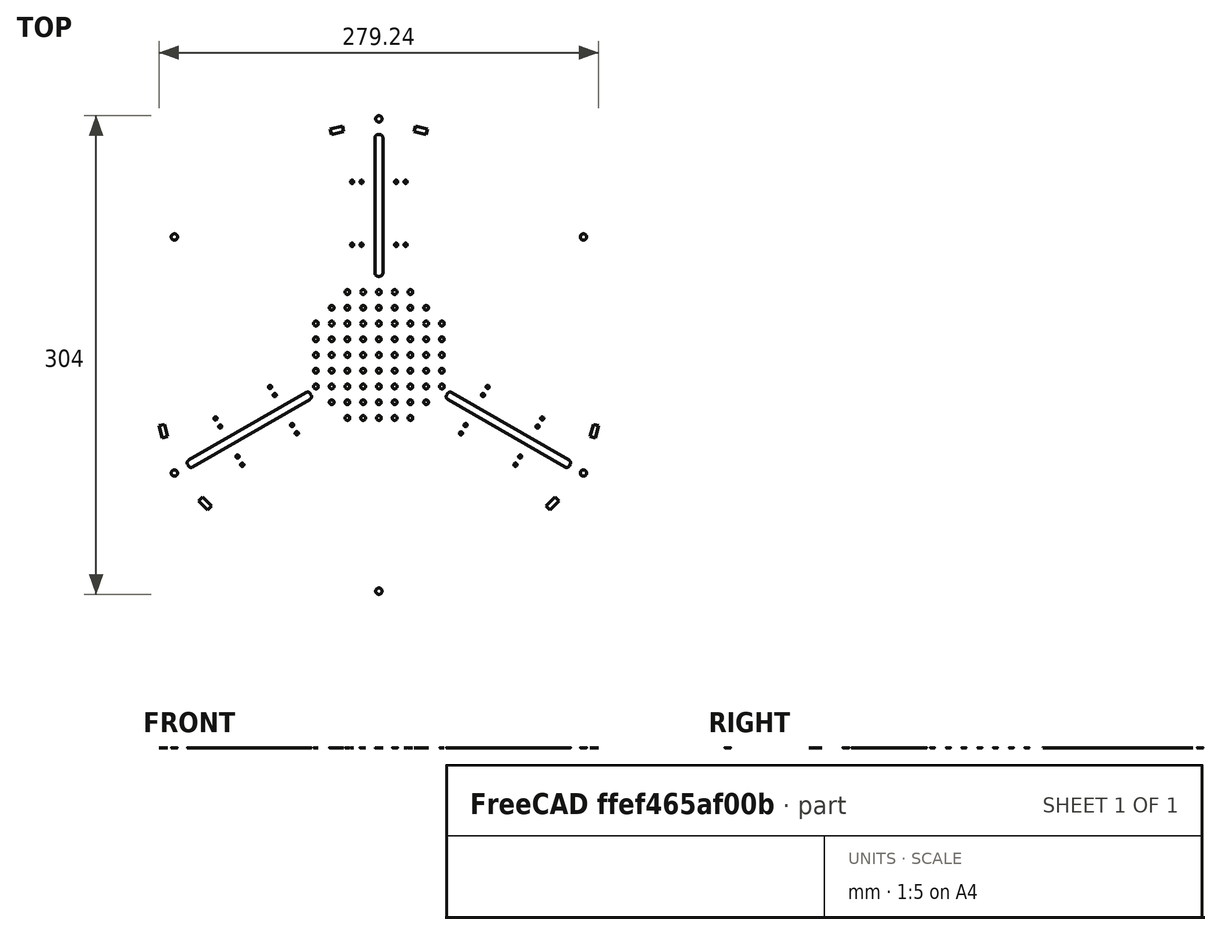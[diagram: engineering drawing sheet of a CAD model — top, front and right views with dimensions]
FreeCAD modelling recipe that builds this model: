
FCSTD DOCUMENT  (FreeCAD 0.16RUnknown)
Label: cylinderBackFace
License: All rights reserved
LicenseURL: http://en.wikipedia.org/wiki/All_rights_reserved
objects: Part::FeaturePython×15, Part::Part2DObjectPython×14, Part::Mirroring×2, Spreadsheet::Sheet×1
note: 31 computed .brp shape members not serialized (recipe doc carries the construction recipe); baked Part::Feature solids carry a one-line shape summary decoded from their .brp

FEATURE [Part::Part2DObjectPython] Circle  label="circleExternal"  # Draft 2D object (typed FeaturePython)
  FirstAngle = 0
  LastAngle = 360
  MakeFace = true
  Radius = 160
  expr: Radius = prefs.circleExternal / 2
FEATURE [Part::Part2DObjectPython] Rectangle  label="slit"  # Draft 2D object (typed FeaturePython)
  ChamferSize = 0
  Columns = 1
  FilletRadius = 2
  Height = 90
  Length = 5
  MakeFace = true
  Placement = pos=(-2.5,50,0) rot=(0,0,1;0rad)
  Rows = 1
  expr: Height = prefs.slitLength
  expr: Placement.Base.x = -prefs.slitWidth / 2
  expr: Length = prefs.slitWidth
  expr: FilletRadius = 2 * prefs.slitWidth / 5
FEATURE [Part::Part2DObjectPython] Circle002  label="screw"  # Draft 2D object (typed FeaturePython)
  FirstAngle = 0
  LastAngle = 0
  MakeFace = true
  Placement = pos=(0,150,0) rot=(0,0,1;0rad)
  Radius = 2
  expr: Placement.Base.y = prefs.circleExternal / 2 - 10
  expr: Radius = prefs.screwDiameter / 2
  expr: Placement.Base.x = 0
FEATURE [Part::FeaturePython] Array001  label="screwArray"  # Draft array (typed FeaturePython)
  Angle = 360
  ArrayType = 1
  Axis = (0,0,1)
  Base = -> Circle002
  Center = (0,0,0)
  Fuse = false
  IntervalAxis = (0,0,0)
  IntervalX = (1,0,0)
  IntervalY = (0,1,0)
  IntervalZ = (0,0,0)
  NumberPolar = 6
  NumberX = 1
  NumberY = 1
  NumberZ = 1
  Placement = pos=(0,0,0) rot=(0,0,1;1.0472rad)
  expr: NumberPolar = Spreadsheet.slitNumber
FEATURE [Spreadsheet::Sheet] Spreadsheet  label="prefs"
  cells = A2=External circle diameter; B2(circleExternal)=320; C2=mm; D2=name = circleExternal; A3=Internal circle diameter; B3(circleInternal)=178; C3=mm; D3=name = circleInternal; A4=Number servo; B4(slitNumber)=6; D4=name = slitNumber; A5=Diameter screw; B5(screwDiameter)=4; C5=mm; D5=name = screwDiameter; A6=Slit width; B6(slitWidth)=5; C6=mm; D6=name = slitWidth; A7=Slit length; B7(slitLength)=90; C7=mm; D7=name = slitLength; A8=Smaller distance from servo border to rotation axis; B8(borderAxisDistance)=10; C8=mm; D8=name = borderAxisDistance
FEATURE [Part::Part2DObjectPython] Circle003  # Draft 2D object (typed FeaturePython)
  FirstAngle = 0
  LastAngle = 0
  MakeFace = true
  Radius = 35
FEATURE [Part::FeaturePython] Array002  label="arcArray"  # Draft array (typed FeaturePython)
  Angle = 360
  ArrayType = 1
  Axis = (0,0,1)
  Center = (0,0,0)
  Fuse = false
  IntervalAxis = (0,0,0)
  IntervalX = (1,0,0)
  IntervalY = (0,1,0)
  IntervalZ = (0,0,0)
  NumberPolar = 3
  NumberX = 1
  NumberY = 1
  NumberZ = 1
FEATURE [Part::Part2DObjectPython] Line  # Draft 2D object (typed FeaturePython)
  Closed = false
  Degree = 1
  MakeFace = true
  Points = (2) [(24.9494,117.378,0),(24.9494,117.378,0)]
FEATURE [Part::Part2DObjectPython] Arc  label="arcExt"  # Draft 2D object (typed FeaturePython)
  FirstAngle = -18.49
  LastAngle = 78.49
  MakeFace = true
  Radius = 125
FEATURE [Part::FeaturePython] Array004  label="arcArrayExt"  # Draft array (typed FeaturePython)
  Angle = 360
  ArrayType = 1
  Axis = (0,0,1)
  Base = -> Arc
  Center = (0,0,0)
  Fuse = false
  IntervalAxis = (0,0,0)
  IntervalX = (1,0,0)
  IntervalY = (0,1,0)
  IntervalZ = (0,0,0)
  NumberPolar = 3
  NumberX = 1
  NumberY = 1
  NumberZ = 1
FEATURE [Part::Part2DObjectPython] Line001  # Draft 2D object (typed FeaturePython)
  ChamferSize = 0
  Closed = false
  End = (-24.9424,43.1862,0)
  FilletRadius = 0
  Length = 79.3
  MakeFace = true
  Points = (2) [(-24.9424,122.486,0),(-24.9424,43.1862,0)]
  Start = (-24.9424,122.486,0)
  Subdivisions = 0
FEATURE [Part::Part2DObjectPython] Line002  # Draft 2D object (typed FeaturePython)
  ChamferSize = 0
  Closed = false
  End = (24.9424,43.1862,0)
  FilletRadius = 0
  Length = 79.3
  MakeFace = true
  Points = (2) [(24.9424,122.486,0),(24.9424,43.1862,0)]
  Start = (24.9424,122.486,0)
  Subdivisions = 0
FEATURE [Part::FeaturePython] Array005  label="side1Array"  # Draft array (typed FeaturePython)
  Angle = 360
  ArrayType = 1
  Axis = (0,0,1)
  Base = -> Line001
  Center = (0,0,0)
  Fuse = false
  IntervalAxis = (0,0,0)
  IntervalX = (1,0,0)
  IntervalY = (0,1,0)
  IntervalZ = (0,0,0)
  NumberPolar = 3
  NumberX = 1
  NumberY = 1
  NumberZ = 1
FEATURE [Part::FeaturePython] Array007  label="side3Array"  # Draft array (typed FeaturePython)
  Angle = 360
  ArrayType = 1
  Axis = (0,0,1)
  Base = -> Line002
  Center = (0,0,0)
  Fuse = false
  IntervalAxis = (0,0,0)
  IntervalX = (1,0,0)
  IntervalY = (0,1,0)
  IntervalZ = (0,0,0)
  NumberPolar = 3
  NumberX = 1
  NumberY = 1
  NumberZ = 1
FEATURE [Part::Part2DObjectPython] Arc001  label="arcInt"  # Draft 2D object (typed FeaturePython)
  FirstAngle = 0
  LastAngle = 60
  MakeFace = true
  Radius = 50
FEATURE [Part::FeaturePython] Array008  label="arcArrayInt"  # Draft array (typed FeaturePython)
  Angle = 360
  ArrayType = 1
  Axis = (0,0,1)
  Base = -> Arc001
  Center = (0,0,0)
  Fuse = false
  IntervalAxis = (0,0,0)
  IntervalX = (1,0,0)
  IntervalY = (0,1,0)
  IntervalZ = (0,0,0)
  NumberPolar = 3
  NumberX = 1
  NumberY = 1
  NumberZ = 1
FEATURE [Part::FeaturePython] Array  label="slitArray"  # Draft array (typed FeaturePython)
  Angle = 360
  ArrayType = 1
  Axis = (0,0,1)
  Base = -> Rectangle
  Center = (0,0,0)
  Fuse = false
  IntervalAxis = (0,0,0)
  IntervalX = (1,0,0)
  IntervalY = (0,1,0)
  IntervalZ = (0,0,0)
  NumberPolar = 3
  NumberX = 1
  NumberY = 1
  NumberZ = 1
FEATURE [Part::Part2DObjectPython] Circle004  label="innerHole1"  # Draft 2D object (typed FeaturePython)
  FirstAngle = 0
  LastAngle = 0
  MakeFace = true
  Placement = pos=(-20,-40,0) rot=(0,0,1;0rad)
  Radius = 1.5
FEATURE [Part::FeaturePython] Array009  label="innerHoleArray1"  # Draft array (typed FeaturePython)
  Angle = 360
  ArrayType = 0
  Axis = (0,0,1)
  Base = -> Circle004
  Center = (0,0,0)
  Fuse = false
  IntervalAxis = (0,0,0)
  IntervalX = (10,0,0)
  IntervalY = (0,10,0)
  IntervalZ = (0,0,0)
  NumberPolar = 1
  NumberX = 5
  NumberY = 9
  NumberZ = 1
FEATURE [Part::Part2DObjectPython] Circle005  label="innerHole2"  # Draft 2D object (typed FeaturePython)
  FirstAngle = 0
  LastAngle = 0
  MakeFace = true
  Placement = pos=(-30,-30,0) rot=(0,0,1;0rad)
  Radius = 1.5
FEATURE [Part::FeaturePython] Array010  label="innerHoleArray2"  # Draft array (typed FeaturePython)
  Angle = 360
  ArrayType = 0
  Axis = (0,0,1)
  Base = -> Circle005
  Center = (0,0,0)
  Fuse = false
  IntervalAxis = (0,0,0)
  IntervalX = (60,0,0)
  IntervalY = (0,10,0)
  IntervalZ = (0,0,0)
  NumberPolar = 1
  NumberX = 2
  NumberY = 7
  NumberZ = 1
FEATURE [Part::Part2DObjectPython] Circle006  label="innerHole3"  # Draft 2D object (typed FeaturePython)
  FirstAngle = 0
  LastAngle = 0
  MakeFace = true
  Placement = pos=(-40,-20,0) rot=(0,0,1;0rad)
  Radius = 1.5
FEATURE [Part::FeaturePython] Array011  label="innerHoleArray3"  # Draft array (typed FeaturePython)
  Angle = 360
  ArrayType = 0
  Axis = (0,0,1)
  Base = -> Circle006
  Center = (0,0,0)
  Fuse = false
  IntervalAxis = (0,0,0)
  IntervalX = (80,0,0)
  IntervalY = (0,10,0)
  IntervalZ = (0,0,0)
  NumberPolar = 1
  NumberX = 2
  NumberY = 5
  NumberZ = 1
FEATURE [Part::Part2DObjectPython] Rectangle001  # Draft 2D object (typed FeaturePython)
  ChamferSize = 0
  Columns = 1
  FilletRadius = 0
  Height = 3.5
  Length = 8
  MakeFace = true
  Placement = pos=(-30,140,0) rot=(0,0,1;0.261799rad)
  Rows = 1
FEATURE [Part::Part2DObjectPython] Circle007  # Draft 2D object (typed FeaturePython)
  FirstAngle = 0
  LastAngle = 0
  MakeFace = true
  Placement = pos=(-17,110,0) rot=(0,0,1;0rad)
  Radius = 1
FEATURE [Part::FeaturePython] Array012  # Draft array (typed FeaturePython)
  Angle = 360
  ArrayType = 0
  Axis = (0,0,1)
  Base = -> Circle007
  Center = (0,0,0)
  Fuse = false
  IntervalAxis = (0,0,0)
  IntervalX = (6,0,0)
  IntervalY = (0,-40,0)
  IntervalZ = (0,0,0)
  NumberPolar = 1
  NumberX = 2
  NumberY = 2
  NumberZ = 1
FEATURE [Part::Mirroring] Part__Mirroring001  label="Array012 (Mirror #2)"
  Base = (0,0,0)
  Normal = (1,0,0)
  Source = -> Array012
FEATURE [Part::FeaturePython] Array013  label="middleHoleArray1"  # Draft array (typed FeaturePython)
  Angle = 360
  ArrayType = 1
  Axis = (0,0,1)
  Base = -> Part__Mirroring001
  Center = (0,0,0)
  Fuse = false
  IntervalAxis = (0,0,0)
  IntervalX = (1,0,0)
  IntervalY = (0,1,0)
  IntervalZ = (0,0,0)
  NumberPolar = 3
  NumberX = 1
  NumberY = 1
  NumberZ = 1
FEATURE [Part::FeaturePython] Array014  label="middleHoleArray2"  # Draft array (typed FeaturePython)
  Angle = 360
  ArrayType = 1
  Axis = (0,0,1)
  Base = -> Array012
  Center = (0,0,0)
  Fuse = false
  IntervalAxis = (0,0,0)
  IntervalX = (1,0,0)
  IntervalY = (0,1,0)
  IntervalZ = (0,0,0)
  NumberPolar = 3
  NumberX = 1
  NumberY = 1
  NumberZ = 1
FEATURE [Part::Mirroring] Part__Mirroring  label="Rectangle001 (Mirror #2)"
  Base = (0,0,0)
  Normal = (1,0,0)
  Source = -> Rectangle001
FEATURE [Part::FeaturePython] Array015  label="rectangleArray1"  # Draft array (typed FeaturePython)
  Angle = 360
  ArrayType = 1
  Axis = (0,0,1)
  Base = -> Rectangle001
  Center = (0,0,0)
  Fuse = false
  IntervalAxis = (0,0,0)
  IntervalX = (1,0,0)
  IntervalY = (0,1,0)
  IntervalZ = (0,0,0)
  NumberPolar = 3
  NumberX = 1
  NumberY = 1
  NumberZ = 1
FEATURE [Part::FeaturePython] Array016  label="rectangleArray2"  # Draft array (typed FeaturePython)
  Angle = 360
  ArrayType = 1
  Axis = (0,0,1)
  Base = -> Part__Mirroring
  Center = (0,0,0)
  Fuse = false
  IntervalAxis = (0,0,0)
  IntervalX = (1,0,0)
  IntervalY = (0,1,0)
  IntervalZ = (0,0,0)
  NumberPolar = 3
  NumberX = 1
  NumberY = 1
  NumberZ = 1
